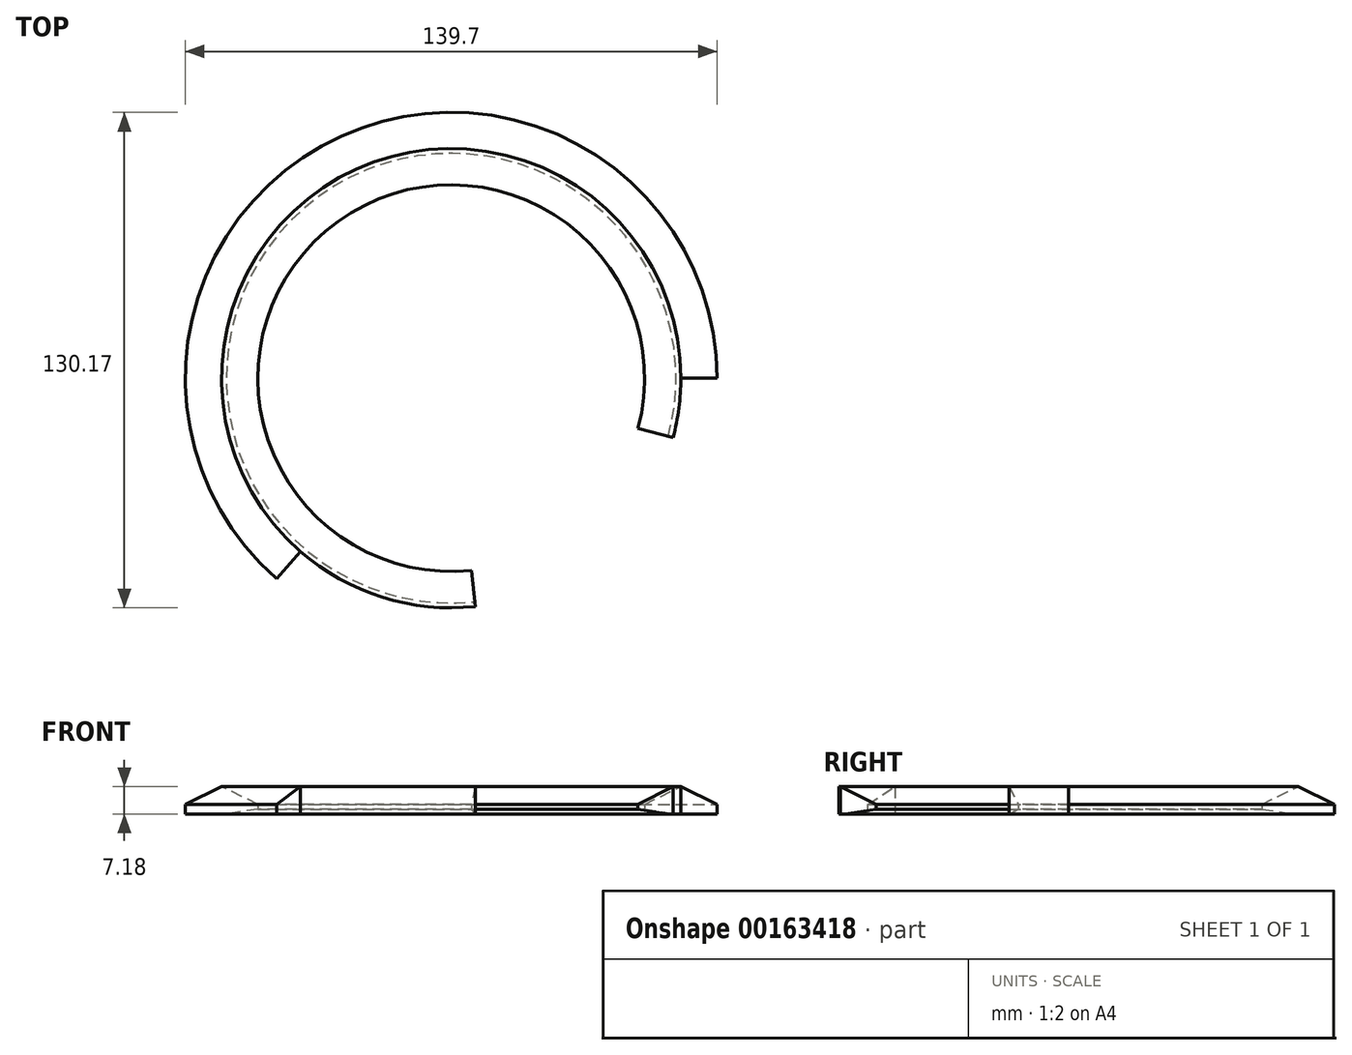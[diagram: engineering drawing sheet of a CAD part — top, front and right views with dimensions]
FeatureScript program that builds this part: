
annotation { "Feature Type Name" : "Feature", "Feature Type Description" : "" }
export const myFeature = defineFeature(function(context is Context, id is Id, definition is map)
    precondition{}
    {
        {
            var Q0;
            Q0=qCreatedBy(makeId("Front.planeOp"),FACE);
            var sketch = newSketch(context, id + "F0", { "sketchPlane" : qUnion([Q0]), "disableImprinting" : false});
            skLineSegment(sketch, "E0", {"start": v(0, 0) * mm, "end": v(60.33, 0) * mm, "construction": true});
            skLineSegment(sketch, "E1", {"start": v(69.85, 9.52) * mm, "end": v(69.85, 12.07) * mm});
            skLineSegment(sketch, "E2", {"start": v(69.85, 12.07) * mm, "end": v(60.33, 16.7) * mm});
            skLineSegment(sketch, "E3", {"start": v(60.33, 16.7) * mm, "end": v(50.8, 12.06) * mm});
            skLineSegment(sketch, "E4", {"start": v(50.8, 12.07) * mm, "end": v(50.8, 10.8) * mm});
            skLineSegment(sketch, "E5", {"start": v(50.8, 10.8) * mm, "end": v(59.06, 9.53) * mm});
            skLineSegment(sketch, "E6", {"start": v(59.06, 9.53) * mm, "end": v(60.33, 9.53) * mm, "construction": true});
            skLineSegment(sketch, "E7", {"start": v(59.06, 9.53) * mm, "end": v(69.85, 9.53) * mm});
            skLineSegment(sketch, "E8", {"start": v(60.33, 0) * mm, "end": v(60.33, 9.53) * mm, "construction": true});
            skLineSegment(sketch, "E9", {"start": v(0, 0) * mm, "end": v(0, 16.7) * mm, "construction": true});
            skSolve(sketch);
        }
        {
            var Q0;
            Q0 = qSketchRegion(id + "F0", true);
            var Q1;
            Q1=sQuery(id+"F0.wireOp",EDGE,"E9");
            revolve(context, id + "F1", {"entities" : qUnion([Q0]), "axis" : qUnion([Q1]), "revolveType" : RevolveType.ONE_DIRECTION, "angle" : 268 * degree});
        }
        {
            var Q0;
            Q0=makeQuery(id+"F1.opRevolve","CAP_FACE",FACE,{"disambiguationData":[OSD([sQuery(id+"F0.wireOp",EDGE,"E1"),sQuery(id+"F0.wireOp",EDGE,"E2"),sQuery(id+"F0.wireOp",EDGE,"E3"),sQuery(id+"F0.wireOp",EDGE,"E4"),sQuery(id+"F0.wireOp",EDGE,"E5"),sQuery(id+"F0.wireOp",EDGE,"E7")])],"isStart":false});
            var sketch = newSketch(context, id + "F2", { "sketchPlane" : qUnion([Q0])});
            skLineSegment(sketch, "E10.0.0", {"start": v(-59.06, 9.53) * mm, "end": v(-50.8, 10.8) * mm});
            skLineSegment(sketch, "E10.0.1", {"start": v(-50.8, 10.8) * mm, "end": v(-50.8, 12.06) * mm});
            skLineSegment(sketch, "E10.0.2", {"start": v(-50.8, 12.06) * mm, "end": v(-60.33, 16.7) * mm});
            skLineSegment(sketch, "E10.0.3", {"start": v(-60.33, 16.7) * mm, "end": v(-69.85, 12.07) * mm});
            skLineSegment(sketch, "E10.0.4", {"start": v(-69.85, 12.06) * mm, "end": v(-69.85, 9.52) * mm});
            skLineSegment(sketch, "E10.0.5", {"start": v(-69.85, 9.53) * mm, "end": v(-59.06, 9.52) * mm});
            skSolve(sketch);
        }
        {
            var Q0;
            Q0 = qSketchRegion(id + "F2", true);
            var Q1;
            Q1=sQuery(id+"F0.wireOp",EDGE,"E9");
            revolve(context, id + "F3", {"operationType" : NewBodyOperationType.ADD, "entities" : qUnion([Q0]), "axis" : qUnion([Q1]), "revolveType" : RevolveType.ONE_DIRECTION, "angle" : 4 * degree});
        }
        {
            var Q0;
            Q0=makeQuery(id+"F0.imprint","IMPRINT",FACE,{"disambiguationData":[TD([[makeQuery(id+"F0.imprint","IMPRINT",EDGE,{"derivedFrom":sQuery(id+"F0.wireOp",EDGE,"E1")}),1.0]])]});
            var sketch = newSketch(context, id + "F4", { "sketchPlane" : qUnion([Q0])});
            skLineSegment(sketch, "E11.0.0", {"start": v(50.8, 10.8) * mm, "end": v(59.06, 9.53) * mm});
            skLineSegment(sketch, "E11.0.1", {"start": v(59.06, 9.53) * mm, "end": v(69.85, 9.53) * mm});
            skLineSegment(sketch, "E11.0.2", {"start": v(69.85, 9.52) * mm, "end": v(69.85, 12.07) * mm});
            skLineSegment(sketch, "E11.0.3", {"start": v(69.85, 12.07) * mm, "end": v(60.33, 16.7) * mm});
            skLineSegment(sketch, "E11.0.4", {"start": v(60.33, 16.7) * mm, "end": v(50.8, 12.06) * mm});
            skLineSegment(sketch, "E11.0.5", {"start": v(50.8, 12.06) * mm, "end": v(50.8, 10.8) * mm});
            skSolve(sketch);
        }
        {
            var Q0;
            Q0 = qSketchRegion(id + "F4", true);
            var Q1;
            Q1=sQuery(id+"F0.wireOp",EDGE,"E9");
            revolve(context, id + "F5", {"operationType" : NewBodyOperationType.ADD, "entities" : qUnion([Q0]), "axis" : qUnion([Q1]), "revolveType" : RevolveType.ONE_DIRECTION, "oppositeDirection" : true, "angle" : 15 * degree});
        }
        {
            var Q0;
            Q0=makeQuery(id+"F3.opRevolve","CAP_FACE",FACE,{"disambiguationData":[OSD([sQuery(id+"F2.wireOp",EDGE,"E10.0.0"),sQuery(id+"F2.wireOp",EDGE,"E10.0.1"),sQuery(id+"F2.wireOp",EDGE,"E10.0.2"),sQuery(id+"F2.wireOp",EDGE,"E10.0.3"),sQuery(id+"F2.wireOp",EDGE,"E10.0.4"),sQuery(id+"F2.wireOp",EDGE,"E10.0.5")])],"isStart":false});
            var sketch = newSketch(context, id + "F6", { "sketchPlane" : qUnion([Q0])});
            skLineSegment(sketch, "E12.0.3", {"start": v(-60.33, 16.7) * mm, "end": v(-69.85, 12.07) * mm});
            skLineSegment(sketch, "E12.0.4", {"start": v(-69.85, 12.06) * mm, "end": v(-69.85, 9.52) * mm});
            skLineSegment(sketch, "E12.0.5", {"start": v(-69.85, 9.53) * mm, "end": v(-60.33, 9.52) * mm});
            skLineSegment(sketch, "E13", {"start": v(-60.33, 16.7) * mm, "end": v(-60.33, 9.52) * mm});
            skSolve(sketch);
        }
        {
            var Q0;
            Q0 = qSketchRegion(id + "F6", true);
            var Q1;
            Q1=sQuery(id+"F0.wireOp",EDGE,"E9");
            revolve(context, id + "F7", {"operationType" : NewBodyOperationType.REMOVE, "entities" : qUnion([Q0]), "axis" : qUnion([Q1]), "revolveType" : RevolveType.ONE_DIRECTION, "oppositeDirection" : true, "angle" : 43 * degree});
        }
        {
            var Q0;
            Q0=makeQuery(id+"F5.opRevolve","CAP_FACE",FACE,{"disambiguationData":[OSD([sQuery(id+"F4.wireOp",EDGE,"E11.0.0"),sQuery(id+"F4.wireOp",EDGE,"E11.0.1"),sQuery(id+"F4.wireOp",EDGE,"E11.0.2"),sQuery(id+"F4.wireOp",EDGE,"E11.0.3"),sQuery(id+"F4.wireOp",EDGE,"E11.0.4"),sQuery(id+"F4.wireOp",EDGE,"E11.0.5")])],"isStart":false});
            var sketch = newSketch(context, id + "F8", { "sketchPlane" : qUnion([Q0])});
            skLineSegment(sketch, "E14.0.2", {"start": v(60.33, 9.53) * mm, "end": v(69.85, 9.53) * mm});
            skLineSegment(sketch, "E14.0.3", {"start": v(69.85, 9.52) * mm, "end": v(69.85, 12.07) * mm});
            skLineSegment(sketch, "E14.0.4", {"start": v(69.85, 12.07) * mm, "end": v(60.33, 16.7) * mm});
            skLineSegment(sketch, "E15", {"start": v(60.33, 16.7) * mm, "end": v(60.33, 9.53) * mm});
            skSolve(sketch);
        }
        {
            var Q0;
            Q0 = qSketchRegion(id + "F8", true);
            var Q1;
            Q1=sQuery(id+"F0.wireOp",EDGE,"E9");
            revolve(context, id + "F9", {"operationType" : NewBodyOperationType.REMOVE, "entities" : qUnion([Q0]), "axis" : qUnion([Q1]), "revolveType" : RevolveType.ONE_DIRECTION, "angle" : 15 * degree});
        }
        {
            var Q0;
            Q0=makeQuery(id+"F3.opRevolve","CAP_FACE",FACE,{"disambiguationData":[OSD([sQuery(id+"F2.wireOp",EDGE,"E10.0.0"),sQuery(id+"F2.wireOp",EDGE,"E10.0.1"),sQuery(id+"F2.wireOp",EDGE,"E10.0.2"),sQuery(id+"F2.wireOp",EDGE,"E10.0.3"),sQuery(id+"F2.wireOp",EDGE,"E10.0.4"),sQuery(id+"F2.wireOp",EDGE,"E10.0.5")])],"isStart":false});
            var sketch = newSketch(context, id + "F10", { "sketchPlane" : qUnion([Q0])});
            skLineSegment(sketch, "E16.0", {"start": v(-60.33, 16.7) * mm, "end": v(-60.33, 9.53) * mm});
            skLineSegment(sketch, "E17.0.0", {"start": v(-50.8, 12.06) * mm, "end": v(-60.33, 16.7) * mm});
            skLineSegment(sketch, "E17.0.2", {"start": v(-60.32, 9.52) * mm, "end": v(-59.06, 9.52) * mm});
            skLineSegment(sketch, "E17.0.3", {"start": v(-59.06, 9.53) * mm, "end": v(-50.8, 10.8) * mm});
            skLineSegment(sketch, "E17.0.4", {"start": v(-50.8, 10.8) * mm, "end": v(-50.8, 12.06) * mm});
            skSolve(sketch);
        }
        {
            var Q0;
            Q0 = qSketchRegion(id + "F10", true);
            var Q1;
            Q1=sQuery(id+"F0.wireOp",EDGE,"E9");
            revolve(context, id + "F11", {"operationType" : NewBodyOperationType.ADD, "entities" : qUnion([Q0]), "axis" : qUnion([Q1]), "revolveType" : RevolveType.ONE_DIRECTION, "angle" : 4 * degree});
        }
    });
